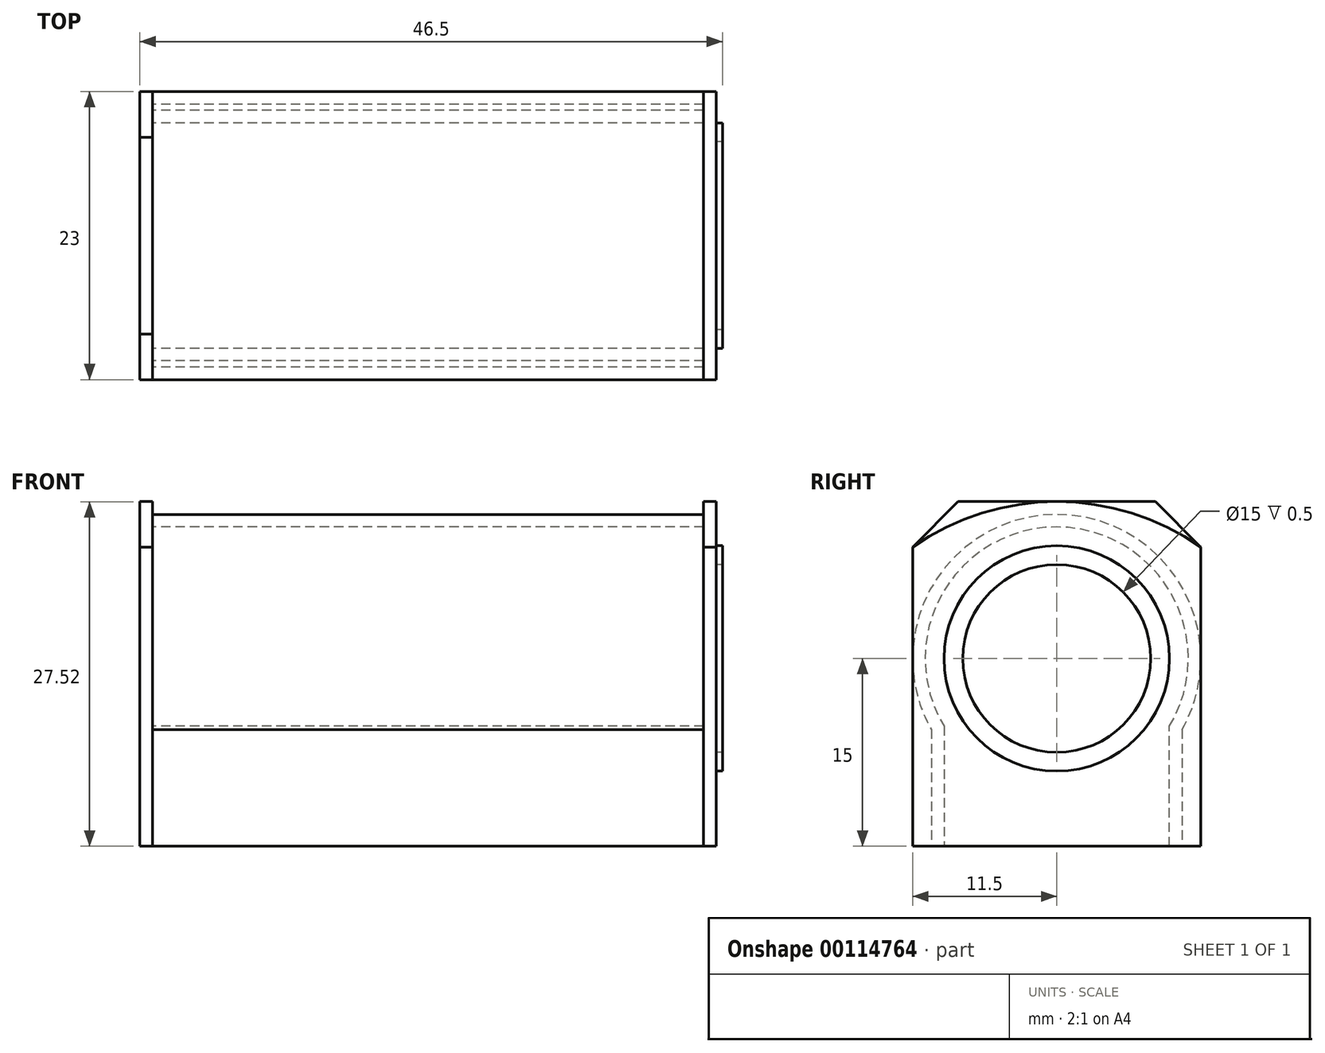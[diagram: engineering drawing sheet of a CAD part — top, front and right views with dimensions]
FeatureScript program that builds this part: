
annotation { "Feature Type Name" : "Feature", "Feature Type Description" : "" }
export const myFeature = defineFeature(function(context is Context, id is Id, definition is map)
    precondition{}
    {
        {
            var Q0;
            Q0=qCreatedBy(makeId("Right.planeOp"),FACE);
            var sketch = newSketch(context, id + "F0", { "sketchPlane" : qUnion([Q0])});
            skCircle(sketch, "E0", {"center": v(0, 15) * mm, "radius": 11.5 * mm});
            skLineSegment(sketch, "E1", {"start": v(-10, 9.32) * mm, "end": v(-10, 0) * mm});
            skLineSegment(sketch, "E2", {"start": v(-10, 0) * mm, "end": v(0, 0) * mm});
            skLineSegment(sketch, "E3.MirrorCS", {"start": v(10, 9.32) * mm, "end": v(10, 0) * mm});
            skLineSegment(sketch, "E4.MirrorCS", {"start": v(10, 0) * mm, "end": v(0, 0) * mm});
            skSolve(sketch);
        }
        {
            var Q0;
            Q0 = qSketchRegion(id + "F0", true);
            extrude(context, id + "F1", {"entities" : qUnion([Q0]), "depth" : 22 * mm, "hasSecondDirection" : true, "secondDirectionOppositeDirection" : true, "secondDirectionDepth" : 22 * mm});
        }
        {
            var Q0;
            Q0=makeQuery(id+"F1.opExtrude","CAP_FACE",FACE,{"disambiguationData":[OSD([sQuery(id+"F0.wireOp",EDGE,"E0"),sQuery(id+"F0.wireOp",EDGE,"E1"),sQuery(id+"F0.wireOp",EDGE,"E2"),sQuery(id+"F0.wireOp",EDGE,"E3.MirrorCS"),sQuery(id+"F0.wireOp",EDGE,"E4.MirrorCS")])],"isStart":false});
            var sketch = newSketch(context, id + "F2", { "sketchPlane" : qUnion([Q0])});
            skLineSegment(sketch, "E5", {"start": v(0, 0) * mm, "end": v(-11.5, 0) * mm});
            skLineSegment(sketch, "E6", {"start": v(-11.5, 0) * mm, "end": v(-11.5, 23.89) * mm});
            skLineSegment(sketch, "E7.MirrorCS", {"start": v(0, 0) * mm, "end": v(11.5, 0) * mm});
            skLineSegment(sketch, "E8.MirrorCS", {"start": v(11.5, 0) * mm, "end": v(11.5, 23.89) * mm});
            skArc(sketch, "E9", {"start": v(11.5, 23.89) * mm, "mid": v(0, 27.52) * mm, "end": v(-11.5, 23.89) * mm});
            skSolve(sketch);
        }
        {
            var Q0;
            Q0 = qSketchRegion(id + "F2", true);
            extrude(context, id + "F3", {"entities" : qUnion([Q0]), "operationType" : NewBodyOperationType.ADD, "depth" : 1 * mm});
        }
        {
            var Q0;
            Q0=makeQuery(id+"F1.opExtrude","CAP_FACE",FACE,{"disambiguationData":[OSD([sQuery(id+"F0.wireOp",EDGE,"E0"),sQuery(id+"F0.wireOp",EDGE,"E1"),sQuery(id+"F0.wireOp",EDGE,"E2"),sQuery(id+"F0.wireOp",EDGE,"E3.MirrorCS"),sQuery(id+"F0.wireOp",EDGE,"E4.MirrorCS")])],"isStart":true});
            var sketch = newSketch(context, id + "F4", { "sketchPlane" : qUnion([Q0])});
            skLineSegment(sketch, "E10.0", {"start": v(-11.5, 15) * mm, "end": v(-11.5, 23.89) * mm});
            skLineSegment(sketch, "E10.1", {"start": v(-11.5, 0) * mm, "end": v(-11.5, 15) * mm});
            skLineSegment(sketch, "E10.2", {"start": v(-11.5, 0) * mm, "end": v(-10, 0) * mm});
            skLineSegment(sketch, "E10.3", {"start": v(10, 0) * mm, "end": v(-10, 0) * mm});
            skLineSegment(sketch, "E10.4", {"start": v(10, 0) * mm, "end": v(11.5, 0) * mm});
            skLineSegment(sketch, "E10.5", {"start": v(11.5, 0) * mm, "end": v(11.5, 15) * mm});
            skLineSegment(sketch, "E10.6", {"start": v(11.5, 15) * mm, "end": v(11.5, 23.89) * mm});
            skArc(sketch, "E11.0", {"start": v(-11.5, 23.89) * mm, "mid": v(0, 27.52) * mm, "end": v(11.5, 23.89) * mm, "construction": true});
            skLineSegment(sketch, "E12", {"start": v(-7.86, 27.52) * mm, "end": v(0, 27.52) * mm});
            skLineSegment(sketch, "E13", {"start": v(-7.86, 27.52) * mm, "end": v(-11.5, 23.89) * mm});
            skLineSegment(sketch, "E14.MirrorCS", {"start": v(7.86, 27.52) * mm, "end": v(0, 27.52) * mm});
            skLineSegment(sketch, "E15.MirrorCS", {"start": v(7.86, 27.52) * mm, "end": v(11.5, 23.89) * mm});
            skSolve(sketch);
        }
        {
            var Q0;
            Q0 = qSketchRegion(id + "F4", true);
            extrude(context, id + "F5", {"entities" : qUnion([Q0]), "operationType" : NewBodyOperationType.ADD, "depth" : 1 * mm});
        }
        {
            var Q0;
            Q0=makeQuery(id+"F5.boolean.opBoolean","MERGE",FACE,{"derivedFrom":[makeQuery(id+"F3.boolean.opBoolean","MERGE",FACE,{"derivedFrom":[makeQuery(id+"F1.opExtrude","SWEPT_FACE",FACE,{"disambiguationData":[OSD([sQuery(id+"F0.wireOp",EDGE,"E2"),sQuery(id+"F0.wireOp",EDGE,"E4.MirrorCS")])]}),makeQuery(id+"F3.opExtrude","SWEPT_FACE",FACE,{"disambiguationData":[OSD([sQuery(id+"F2.wireOp",EDGE,"E5"),sQuery(id+"F2.wireOp",EDGE,"E7.MirrorCS")])]})]}),makeQuery(id+"F5.opExtrude","SWEPT_FACE",FACE,{"disambiguationData":[OSD([sQuery(id+"F4.wireOp",EDGE,"E10.2"),sQuery(id+"F4.wireOp",EDGE,"E10.3"),sQuery(id+"F4.wireOp",EDGE,"E10.4")])]})]});
            shell(context, id + "F6", {"entities" : qUnion([Q0]), "thickness" : 1 * mm});
        }
        {
            var Q0;
            Q0=makeQuery(id+"F3.opExtrude","CAP_FACE",FACE,{"disambiguationData":[OSD([sQuery(id+"F2.wireOp",EDGE,"E5"),sQuery(id+"F2.wireOp",EDGE,"E6"),sQuery(id+"F2.wireOp",EDGE,"E7.MirrorCS"),sQuery(id+"F2.wireOp",EDGE,"E8.MirrorCS"),sQuery(id+"F2.wireOp",EDGE,"E9")])],"isStart":false});
            var sketch = newSketch(context, id + "F7", { "sketchPlane" : qUnion([Q0])});
            skArc(sketch, "E16.0", {"start": v(11.5, 15) * mm, "mid": v(0, 26.5) * mm, "end": v(-11.5, 15) * mm, "construction": true});
            skCircle(sketch, "E17", {"center": v(0, 15) * mm, "radius": 9 * mm});
            skCircle(sketch, "E18", {"center": v(0, 15) * mm, "radius": 7.5 * mm});
            skSolve(sketch);
        }
        {
            var Q0;
            Q0 = qSketchRegion(id + "F7", true);
            var Q1;
            Q1 = qConstructionFilter(qBodyType(qCreatedBy(id + "F7" ,EDGE), BodyType.WIRE), ConstructionObject.NO);
            extrude(context, id + "F8", {"entities" : qUnion([Q0]), "operationType" : NewBodyOperationType.ADD, "surfaceEntities" : qUnion([Q1]), "depth" : 0.5 * mm});
        }
    });
